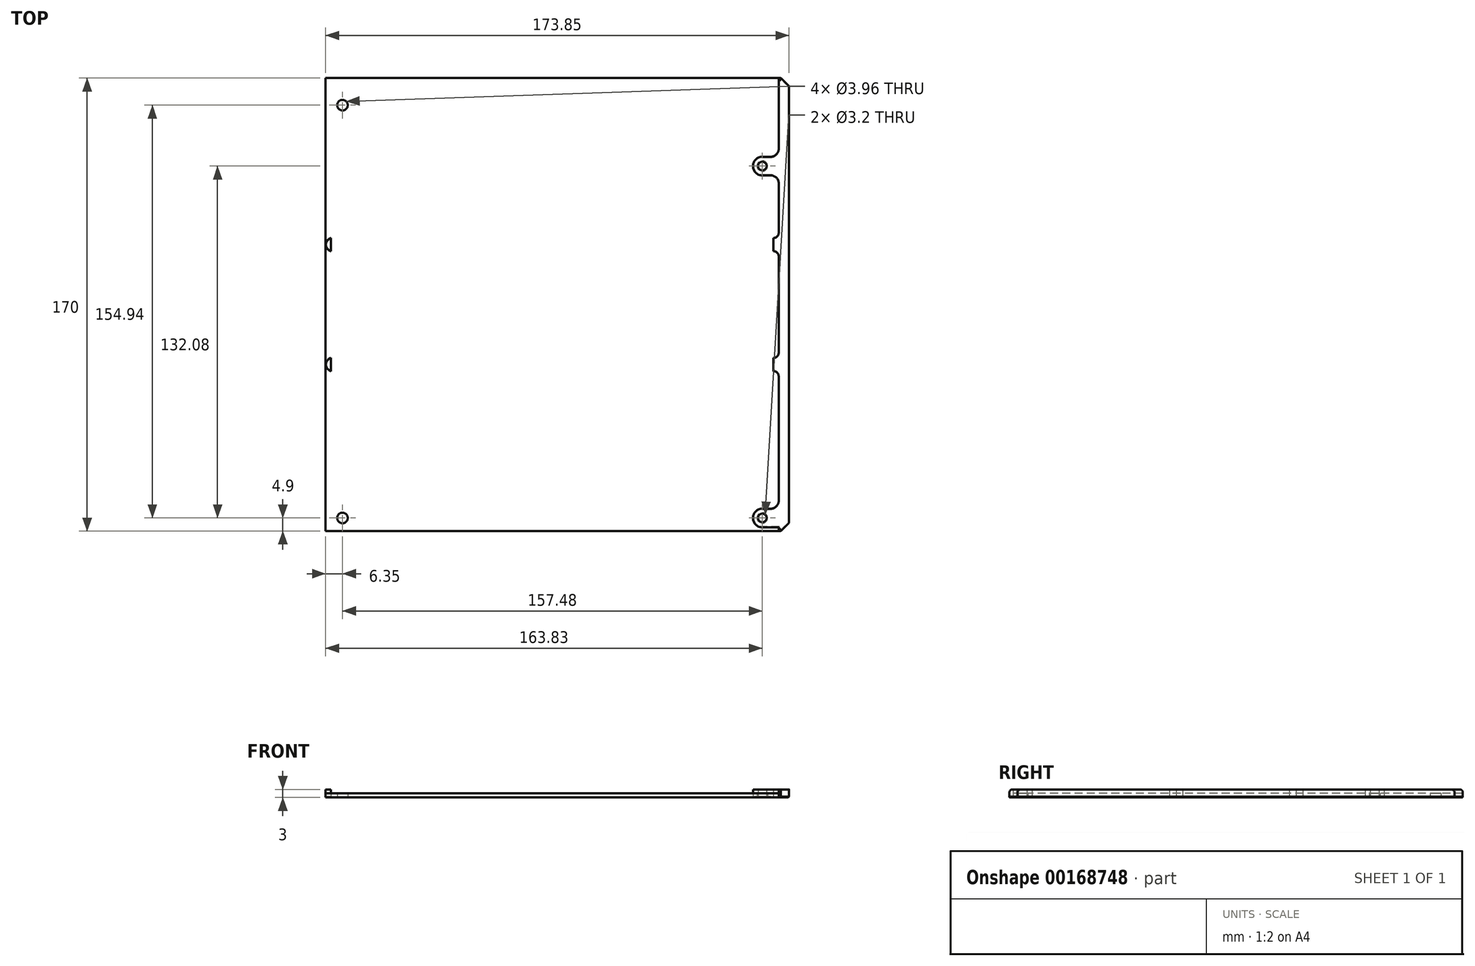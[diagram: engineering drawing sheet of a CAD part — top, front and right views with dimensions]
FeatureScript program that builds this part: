
annotation { "Feature Type Name" : "Feature", "Feature Type Description" : "" }
export const myFeature = defineFeature(function(context is Context, id is Id, definition is map)
    precondition{}
    {
        {
            var Q0;
            Q0=qCreatedBy(makeId("Top.planeOp"),FACE);
            var sketch = newSketch(context, id + "F8", { "sketchPlane" : qUnion([Q0])});
            skLineSegment(sketch, "E0.bottom", {"start": v(85, 85) * mm, "end": v(-85, 85) * mm});
            skLineSegment(sketch, "E0.top", {"start": v(85, -85) * mm, "end": v(-85, -85) * mm});
            skLineSegment(sketch, "E0.left", {"start": v(85, 85) * mm, "end": v(85, -85) * mm});
            skLineSegment(sketch, "E0.right", {"start": v(-85, 85) * mm, "end": v(-85, -85) * mm});
            skPoint(sketch, "E0.middle", {"position": v(0, 0) * mm});
            skCircle(sketch, "E1", {"center": v(-78.65, 74.84) * mm, "radius": 1.98 * mm});
            skCircle(sketch, "E2", {"center": v(-78.65, -80.1) * mm, "radius": 1.98 * mm});
            skCircle(sketch, "E3", {"center": v(78.83, -80.1) * mm, "radius": 1.98 * mm});
            skCircle(sketch, "E4", {"center": v(78.83, 51.98) * mm, "radius": 1.98 * mm});
            skLineSegment(sketch, "E5", {"start": v(-78.65, 74.84) * mm, "end": v(85, 74.84) * mm, "construction": true});
            skSolve(sketch);
        }
        {
            var Q0;
            Q0=qCreatedBy(makeId("Top.planeOp"),FACE);
            var sketch = newSketch(context, id + "F0", { "sketchPlane" : qUnion([Q0])});
            skPoint(sketch, "E6.0", {"position": v(78.83, 51.98) * mm});
            skPoint(sketch, "E6.1", {"position": v(-78.65, 74.84) * mm});
            skPoint(sketch, "E6.2", {"position": v(-78.65, -80.1) * mm});
            skPoint(sketch, "E6.3", {"position": v(78.83, -80.1) * mm});
            skLineSegment(sketch, "E6.4", {"start": v(-85, 85) * mm, "end": v(-85, -85) * mm, "construction": true});
            skLineSegment(sketch, "E7.0", {"start": v(85, 85) * mm, "end": v(85, -85) * mm, "construction": true});
            skArc(sketch, "E8", {"start": v(-78.65, 78.34) * mm, "mid": v(-75.15, 74.84) * mm, "end": v(-78.65, 71.34) * mm});
            skLineSegment(sketch, "E9", {"start": v(-78.65, 78.34) * mm, "end": v(-85, 78.34) * mm});
            skLineSegment(sketch, "E10", {"start": v(-85, 78.34) * mm, "end": v(-85, 85) * mm});
            skLineSegment(sketch, "E11", {"start": v(-78.65, 71.34) * mm, "end": v(-85, 71.34) * mm});
            skArc(sketch, "E12", {"start": v(-78.65, -76.6) * mm, "mid": v(-75.15, -80.1) * mm, "end": v(-78.65, -83.6) * mm});
            skArc(sketch, "E13", {"start": v(78.83, 55.48) * mm, "mid": v(75.33, 51.98) * mm, "end": v(78.83, 48.48) * mm});
            skArc(sketch, "E14", {"start": v(78.83, -76.6) * mm, "mid": v(75.33, -80.1) * mm, "end": v(78.83, -83.6) * mm});
            skCircle(sketch, "E15", {"center": v(-78.65, 74.84) * mm, "radius": 1.6 * mm});
            skCircle(sketch, "E16", {"center": v(78.83, 51.98) * mm, "radius": 1.6 * mm});
            skCircle(sketch, "E17", {"center": v(-78.65, -80.1) * mm, "radius": 1.6 * mm});
            skCircle(sketch, "E18", {"center": v(78.83, -80.1) * mm, "radius": 1.6 * mm});
            skLineSegment(sketch, "E19", {"start": v(-78.65, -76.6) * mm, "end": v(-85, -76.6) * mm});
            skLineSegment(sketch, "E20", {"start": v(-85, -76.6) * mm, "end": v(-85, 71.34) * mm});
            skLineSegment(sketch, "E21", {"start": v(78.83, 55.48) * mm, "end": v(85, 55.48) * mm});
            skLineSegment(sketch, "E22", {"start": v(85, 55.48) * mm, "end": v(85, 85) * mm});
            skLineSegment(sketch, "E23", {"start": v(78.83, -76.6) * mm, "end": v(85, -76.6) * mm});
            skLineSegment(sketch, "E24", {"start": v(78.83, 48.48) * mm, "end": v(85, 48.48) * mm});
            skLineSegment(sketch, "E25", {"start": v(85, 48.48) * mm, "end": v(85, -76.6) * mm});
            skLineSegment(sketch, "E26", {"start": v(78.83, -83.6) * mm, "end": v(85, -83.6) * mm});
            skLineSegment(sketch, "E27", {"start": v(-78.65, -83.6) * mm, "end": v(-85, -83.6) * mm});
            skLineSegment(sketch, "E28", {"start": v(-85, 85) * mm, "end": v(-88.85, 85) * mm});
            skLineSegment(sketch, "E29", {"start": v(-88.85, 85) * mm, "end": v(-88.85, -85) * mm});
            skLineSegment(sketch, "E30", {"start": v(85, 85) * mm, "end": v(88.85, 85) * mm});
            skLineSegment(sketch, "E31", {"start": v(88.85, 85) * mm, "end": v(88.85, -85) * mm});
            skLineSegment(sketch, "E32", {"start": v(85, -83.6) * mm, "end": v(85, -85) * mm});
            skLineSegment(sketch, "E33", {"start": v(88.85, -85) * mm, "end": v(85, -85) * mm});
            skLineSegment(sketch, "E34", {"start": v(-85, -83.6) * mm, "end": v(-85, -85) * mm});
            skLineSegment(sketch, "E35", {"start": v(-88.85, -85) * mm, "end": v(-85, -85) * mm});
            skLineSegment(sketch, "E36", {"start": v(-85, 25) * mm, "end": v(-83, 25) * mm});
            skLineSegment(sketch, "E37", {"start": v(-83, 25) * mm, "end": v(-83, 20) * mm});
            skLineSegment(sketch, "E38", {"start": v(-83, 20) * mm, "end": v(-85, 20) * mm});
            skLineSegment(sketch, "E39", {"start": v(-85, -20) * mm, "end": v(-83, -20) * mm});
            skLineSegment(sketch, "E40", {"start": v(-83, -20) * mm, "end": v(-83, -25) * mm});
            skLineSegment(sketch, "E41", {"start": v(-83, -25) * mm, "end": v(-85, -25) * mm});
            skLineSegment(sketch, "E42.MirrorCS", {"start": v(85, 25) * mm, "end": v(83, 25) * mm});
            skLineSegment(sketch, "E43.MirrorCS", {"start": v(83, 25) * mm, "end": v(83, 20) * mm});
            skLineSegment(sketch, "E44.MirrorCS", {"start": v(83, 20) * mm, "end": v(85, 20) * mm});
            skLineSegment(sketch, "E45.MirrorCS", {"start": v(85, -20) * mm, "end": v(83, -20) * mm});
            skLineSegment(sketch, "E46.MirrorCS", {"start": v(83, -20) * mm, "end": v(83, -25) * mm});
            skLineSegment(sketch, "E47.MirrorCS", {"start": v(83, -25) * mm, "end": v(85, -25) * mm});
            skSolve(sketch);
        }
        {
            var Q0;
            Q0=makeQuery(id+"F0.imprint","IMPRINT",FACE,{"disambiguationData":[TD([[makeQuery(id+"F0.imprint","IMPRINT",EDGE,{"derivedFrom":sQuery(id+"F0.wireOp",EDGE,"E8")}),-1.0]])]});
            var Q1;
            Q1=makeQuery(id+"F0.imprint","IMPRINT",FACE,{"disambiguationData":[TD([[makeQuery(id+"F0.imprint","IMPRINT",EDGE,{"derivedFrom":sQuery(id+"F0.wireOp",EDGE,"E13")}),1.0]])]});
            var Q2;
            {var subQ0=sQuery(id+"F0.wireOp",EDGE,"E36");Q2=makeQuery(id+"F0.imprint","IMPRINT",FACE,{"disambiguationData":[TD([[makeQuery(id+"F0.imprint","IMPRINT",EDGE,{"derivedFrom":subQ0}),-1.0]])]});}
            var Q3;
            {var subQ0=sQuery(id+"F0.wireOp",EDGE,"E39");Q3=makeQuery(id+"F0.imprint","IMPRINT",FACE,{"disambiguationData":[TD([[makeQuery(id+"F0.imprint","IMPRINT",EDGE,{"derivedFrom":subQ0}),-1.0]])]});}
            var Q4;
            {var subQ0=sQuery(id+"F0.wireOp",EDGE,"E42.MirrorCS");Q4=makeQuery(id+"F0.imprint","IMPRINT",FACE,{"disambiguationData":[TD([[makeQuery(id+"F0.imprint","IMPRINT",EDGE,{"derivedFrom":subQ0}),1.0]])]});}
            var Q5;
            {var subQ0=sQuery(id+"F0.wireOp",EDGE,"E45.MirrorCS");Q5=makeQuery(id+"F0.imprint","IMPRINT",FACE,{"disambiguationData":[TD([[makeQuery(id+"F0.imprint","IMPRINT",EDGE,{"derivedFrom":subQ0}),1.0]])]});}
            extrude(context, id + "F1", {"entities" : qUnion([Q0, Q1, Q2, Q3, Q4, Q5]), "depth" : 3 * mm});
        }
        {
            var Q0;
            Q0=makeQuery(id+"F1.opExtrude","SWEPT_EDGE",EDGE,{"disambiguationData":[OSD([sQuery(id+"F0.wireOp",EDGE,"E29"),sQuery(id+"F0.wireOp",EDGE,"E35")])]});
            var Q1;
            Q1=makeQuery(id+"F1.opExtrude","SWEPT_EDGE",EDGE,{"disambiguationData":[OSD([sQuery(id+"F0.wireOp",EDGE,"E31"),sQuery(id+"F0.wireOp",EDGE,"E33")])]});
            var Q2;
            Q2=makeQuery(id+"F1.opExtrude","SWEPT_EDGE",EDGE,{"disambiguationData":[OSD([sQuery(id+"F0.wireOp",EDGE,"E28"),sQuery(id+"F0.wireOp",EDGE,"E29")])]});
            var Q3;
            Q3=makeQuery(id+"F1.opExtrude","SWEPT_EDGE",EDGE,{"disambiguationData":[OSD([sQuery(id+"F0.wireOp",EDGE,"E30"),sQuery(id+"F0.wireOp",EDGE,"E31")])]});
            chamfer(context, id + "F2", {"entities" : qUnion([Q0, Q1, Q2, Q3]), "width" : 3 * mm});
        }
        {
            var Q0;
            Q0=makeQuery(id+"F1.opExtrude","CAP_EDGE",EDGE,{"disambiguationData":[OSD([sQuery(id+"F0.wireOp",EDGE,"E33")])],"isStart":false});
            var Q1;
            Q1=makeQuery(id+"F1.opExtrude","CAP_EDGE",EDGE,{"disambiguationData":[OSD([sQuery(id+"F0.wireOp",EDGE,"E35")])],"isStart":false});
            var Q2;
            {var subQ0=sQuery(id+"F0.wireOp",EDGE,"E35");var subQ1=sQuery(id+"F0.wireOp",EDGE,"E29");Q2=makeQuery(id+"F2.opChamfer","BLEND_EDGE",EDGE,{"blendedFrom":[makeQuery(id+"F1.opExtrude","SWEPT_EDGE",EDGE,{"disambiguationData":[OSD([subQ1,subQ0])]}),makeQuery(id+"F1.opExtrude","CAP_FACE",FACE,{"disambiguationData":[OSD([sQuery(id+"F0.wireOp",EDGE,"E8"),sQuery(id+"F0.wireOp",EDGE,"E9"),sQuery(id+"F0.wireOp",EDGE,"E10"),sQuery(id+"F0.wireOp",EDGE,"E11"),sQuery(id+"F0.wireOp",EDGE,"E12"),sQuery(id+"F0.wireOp",EDGE,"E15"),sQuery(id+"F0.wireOp",EDGE,"E17"),sQuery(id+"F0.wireOp",EDGE,"E19"),sQuery(id+"F0.wireOp",EDGE,"E20"),sQuery(id+"F0.wireOp",EDGE,"E27"),sQuery(id+"F0.wireOp",EDGE,"E28"),subQ1,sQuery(id+"F0.wireOp",EDGE,"E34"),subQ0,sQuery(id+"F0.wireOp",EDGE,"E36"),sQuery(id+"F0.wireOp",EDGE,"E37"),sQuery(id+"F0.wireOp",EDGE,"E38"),sQuery(id+"F0.wireOp",EDGE,"E39"),sQuery(id+"F0.wireOp",EDGE,"E40"),sQuery(id+"F0.wireOp",EDGE,"E41")])],"isStart":false})],"blendedInto":[makeQuery(id+"F1.opExtrude","CAP_FACE",FACE,{"disambiguationData":[OSD([sQuery(id+"F0.wireOp",EDGE,"E8"),sQuery(id+"F0.wireOp",EDGE,"E9"),sQuery(id+"F0.wireOp",EDGE,"E10"),sQuery(id+"F0.wireOp",EDGE,"E11"),sQuery(id+"F0.wireOp",EDGE,"E12"),sQuery(id+"F0.wireOp",EDGE,"E15"),sQuery(id+"F0.wireOp",EDGE,"E17"),sQuery(id+"F0.wireOp",EDGE,"E19"),sQuery(id+"F0.wireOp",EDGE,"E20"),sQuery(id+"F0.wireOp",EDGE,"E27"),sQuery(id+"F0.wireOp",EDGE,"E28"),subQ1,sQuery(id+"F0.wireOp",EDGE,"E34"),subQ0,sQuery(id+"F0.wireOp",EDGE,"E36"),sQuery(id+"F0.wireOp",EDGE,"E37"),sQuery(id+"F0.wireOp",EDGE,"E38"),sQuery(id+"F0.wireOp",EDGE,"E39"),sQuery(id+"F0.wireOp",EDGE,"E40"),sQuery(id+"F0.wireOp",EDGE,"E41")])],"isStart":false})]});}
            var Q3;
            {var subQ0=sQuery(id+"F0.wireOp",EDGE,"E33");var subQ1=sQuery(id+"F0.wireOp",EDGE,"E31");Q3=makeQuery(id+"F2.opChamfer","BLEND_EDGE",EDGE,{"blendedFrom":[makeQuery(id+"F1.opExtrude","SWEPT_EDGE",EDGE,{"disambiguationData":[OSD([subQ1,subQ0])]}),makeQuery(id+"F1.opExtrude","CAP_FACE",FACE,{"disambiguationData":[OSD([sQuery(id+"F0.wireOp",EDGE,"E13"),sQuery(id+"F0.wireOp",EDGE,"E14"),sQuery(id+"F0.wireOp",EDGE,"E16"),sQuery(id+"F0.wireOp",EDGE,"E18"),sQuery(id+"F0.wireOp",EDGE,"E21"),sQuery(id+"F0.wireOp",EDGE,"E22"),sQuery(id+"F0.wireOp",EDGE,"E23"),sQuery(id+"F0.wireOp",EDGE,"E24"),sQuery(id+"F0.wireOp",EDGE,"E25"),sQuery(id+"F0.wireOp",EDGE,"E26"),sQuery(id+"F0.wireOp",EDGE,"E30"),subQ1,sQuery(id+"F0.wireOp",EDGE,"E32"),subQ0,sQuery(id+"F0.wireOp",EDGE,"E42.MirrorCS"),sQuery(id+"F0.wireOp",EDGE,"E43.MirrorCS"),sQuery(id+"F0.wireOp",EDGE,"E44.MirrorCS"),sQuery(id+"F0.wireOp",EDGE,"E45.MirrorCS"),sQuery(id+"F0.wireOp",EDGE,"E46.MirrorCS"),sQuery(id+"F0.wireOp",EDGE,"E47.MirrorCS")])],"isStart":false})],"blendedInto":[makeQuery(id+"F1.opExtrude","CAP_FACE",FACE,{"disambiguationData":[OSD([sQuery(id+"F0.wireOp",EDGE,"E13"),sQuery(id+"F0.wireOp",EDGE,"E14"),sQuery(id+"F0.wireOp",EDGE,"E16"),sQuery(id+"F0.wireOp",EDGE,"E18"),sQuery(id+"F0.wireOp",EDGE,"E21"),sQuery(id+"F0.wireOp",EDGE,"E22"),sQuery(id+"F0.wireOp",EDGE,"E23"),sQuery(id+"F0.wireOp",EDGE,"E24"),sQuery(id+"F0.wireOp",EDGE,"E25"),sQuery(id+"F0.wireOp",EDGE,"E26"),sQuery(id+"F0.wireOp",EDGE,"E30"),subQ1,sQuery(id+"F0.wireOp",EDGE,"E32"),subQ0,sQuery(id+"F0.wireOp",EDGE,"E42.MirrorCS"),sQuery(id+"F0.wireOp",EDGE,"E43.MirrorCS"),sQuery(id+"F0.wireOp",EDGE,"E44.MirrorCS"),sQuery(id+"F0.wireOp",EDGE,"E45.MirrorCS"),sQuery(id+"F0.wireOp",EDGE,"E46.MirrorCS"),sQuery(id+"F0.wireOp",EDGE,"E47.MirrorCS")])],"isStart":false})]});}
            var Q4;
            Q4=makeQuery(id+"F1.opExtrude","CAP_EDGE",EDGE,{"disambiguationData":[OSD([sQuery(id+"F0.wireOp",EDGE,"E28")])],"isStart":false});
            var Q5;
            {var subQ0=sQuery(id+"F0.wireOp",EDGE,"E29");var subQ1=sQuery(id+"F0.wireOp",EDGE,"E28");Q5=makeQuery(id+"F2.opChamfer","BLEND_EDGE",EDGE,{"blendedFrom":[makeQuery(id+"F1.opExtrude","SWEPT_EDGE",EDGE,{"disambiguationData":[OSD([subQ1,subQ0])]}),makeQuery(id+"F1.opExtrude","CAP_FACE",FACE,{"disambiguationData":[OSD([sQuery(id+"F0.wireOp",EDGE,"E8"),sQuery(id+"F0.wireOp",EDGE,"E9"),sQuery(id+"F0.wireOp",EDGE,"E10"),sQuery(id+"F0.wireOp",EDGE,"E11"),sQuery(id+"F0.wireOp",EDGE,"E12"),sQuery(id+"F0.wireOp",EDGE,"E15"),sQuery(id+"F0.wireOp",EDGE,"E17"),sQuery(id+"F0.wireOp",EDGE,"E19"),sQuery(id+"F0.wireOp",EDGE,"E20"),sQuery(id+"F0.wireOp",EDGE,"E27"),subQ1,subQ0,sQuery(id+"F0.wireOp",EDGE,"E34"),sQuery(id+"F0.wireOp",EDGE,"E35"),sQuery(id+"F0.wireOp",EDGE,"E36"),sQuery(id+"F0.wireOp",EDGE,"E37"),sQuery(id+"F0.wireOp",EDGE,"E38"),sQuery(id+"F0.wireOp",EDGE,"E39"),sQuery(id+"F0.wireOp",EDGE,"E40"),sQuery(id+"F0.wireOp",EDGE,"E41")])],"isStart":false})],"blendedInto":[makeQuery(id+"F1.opExtrude","CAP_FACE",FACE,{"disambiguationData":[OSD([sQuery(id+"F0.wireOp",EDGE,"E8"),sQuery(id+"F0.wireOp",EDGE,"E9"),sQuery(id+"F0.wireOp",EDGE,"E10"),sQuery(id+"F0.wireOp",EDGE,"E11"),sQuery(id+"F0.wireOp",EDGE,"E12"),sQuery(id+"F0.wireOp",EDGE,"E15"),sQuery(id+"F0.wireOp",EDGE,"E17"),sQuery(id+"F0.wireOp",EDGE,"E19"),sQuery(id+"F0.wireOp",EDGE,"E20"),sQuery(id+"F0.wireOp",EDGE,"E27"),subQ1,subQ0,sQuery(id+"F0.wireOp",EDGE,"E34"),sQuery(id+"F0.wireOp",EDGE,"E35"),sQuery(id+"F0.wireOp",EDGE,"E36"),sQuery(id+"F0.wireOp",EDGE,"E37"),sQuery(id+"F0.wireOp",EDGE,"E38"),sQuery(id+"F0.wireOp",EDGE,"E39"),sQuery(id+"F0.wireOp",EDGE,"E40"),sQuery(id+"F0.wireOp",EDGE,"E41")])],"isStart":false})]});}
            var Q6;
            {var subQ0=sQuery(id+"F0.wireOp",EDGE,"E31");var subQ1=sQuery(id+"F0.wireOp",EDGE,"E30");Q6=makeQuery(id+"F2.opChamfer","BLEND_EDGE",EDGE,{"blendedFrom":[makeQuery(id+"F1.opExtrude","SWEPT_EDGE",EDGE,{"disambiguationData":[OSD([subQ1,subQ0])]}),makeQuery(id+"F1.opExtrude","CAP_FACE",FACE,{"disambiguationData":[OSD([sQuery(id+"F0.wireOp",EDGE,"E13"),sQuery(id+"F0.wireOp",EDGE,"E14"),sQuery(id+"F0.wireOp",EDGE,"E16"),sQuery(id+"F0.wireOp",EDGE,"E18"),sQuery(id+"F0.wireOp",EDGE,"E21"),sQuery(id+"F0.wireOp",EDGE,"E22"),sQuery(id+"F0.wireOp",EDGE,"E23"),sQuery(id+"F0.wireOp",EDGE,"E24"),sQuery(id+"F0.wireOp",EDGE,"E25"),sQuery(id+"F0.wireOp",EDGE,"E26"),subQ1,subQ0,sQuery(id+"F0.wireOp",EDGE,"E32"),sQuery(id+"F0.wireOp",EDGE,"E33"),sQuery(id+"F0.wireOp",EDGE,"E42.MirrorCS"),sQuery(id+"F0.wireOp",EDGE,"E43.MirrorCS"),sQuery(id+"F0.wireOp",EDGE,"E44.MirrorCS"),sQuery(id+"F0.wireOp",EDGE,"E45.MirrorCS"),sQuery(id+"F0.wireOp",EDGE,"E46.MirrorCS"),sQuery(id+"F0.wireOp",EDGE,"E47.MirrorCS")])],"isStart":false})],"blendedInto":[makeQuery(id+"F1.opExtrude","CAP_FACE",FACE,{"disambiguationData":[OSD([sQuery(id+"F0.wireOp",EDGE,"E13"),sQuery(id+"F0.wireOp",EDGE,"E14"),sQuery(id+"F0.wireOp",EDGE,"E16"),sQuery(id+"F0.wireOp",EDGE,"E18"),sQuery(id+"F0.wireOp",EDGE,"E21"),sQuery(id+"F0.wireOp",EDGE,"E22"),sQuery(id+"F0.wireOp",EDGE,"E23"),sQuery(id+"F0.wireOp",EDGE,"E24"),sQuery(id+"F0.wireOp",EDGE,"E25"),sQuery(id+"F0.wireOp",EDGE,"E26"),subQ1,subQ0,sQuery(id+"F0.wireOp",EDGE,"E32"),sQuery(id+"F0.wireOp",EDGE,"E33"),sQuery(id+"F0.wireOp",EDGE,"E42.MirrorCS"),sQuery(id+"F0.wireOp",EDGE,"E43.MirrorCS"),sQuery(id+"F0.wireOp",EDGE,"E44.MirrorCS"),sQuery(id+"F0.wireOp",EDGE,"E45.MirrorCS"),sQuery(id+"F0.wireOp",EDGE,"E46.MirrorCS"),sQuery(id+"F0.wireOp",EDGE,"E47.MirrorCS")])],"isStart":false})]});}
            var Q7;
            Q7=makeQuery(id+"F1.opExtrude","CAP_EDGE",EDGE,{"disambiguationData":[OSD([sQuery(id+"F0.wireOp",EDGE,"E30")])],"isStart":false});
            fillet(context, id + "F3", {"entities" : qUnion([Q0, Q1, Q2, Q3, Q4, Q5, Q6, Q7]), "radius" : 1 * mm, "allowEdgeOverflow" : false});
        }
        {
            var Q0;
            Q0=makeQuery(id+"F1.opExtrude","SWEPT_EDGE",EDGE,{"disambiguationData":[OSD([sQuery(id+"F0.wireOp",EDGE,"E19"),sQuery(id+"F0.wireOp",EDGE,"E20")])]});
            var Q1;
            Q1=makeQuery(id+"F1.opExtrude","SWEPT_EDGE",EDGE,{"disambiguationData":[OSD([sQuery(id+"F0.wireOp",EDGE,"E23"),sQuery(id+"F0.wireOp",EDGE,"E25")])]});
            var Q2;
            Q2=makeQuery(id+"F1.opExtrude","SWEPT_EDGE",EDGE,{"disambiguationData":[OSD([sQuery(id+"F0.wireOp",EDGE,"E24"),sQuery(id+"F0.wireOp",EDGE,"E25")])]});
            var Q3;
            Q3=makeQuery(id+"F1.opExtrude","SWEPT_EDGE",EDGE,{"disambiguationData":[OSD([sQuery(id+"F0.wireOp",EDGE,"E11"),sQuery(id+"F0.wireOp",EDGE,"E20")])]});
            var Q4;
            Q4=makeQuery(id+"F1.opExtrude","SWEPT_EDGE",EDGE,{"disambiguationData":[OSD([sQuery(id+"F0.wireOp",EDGE,"E9"),sQuery(id+"F0.wireOp",EDGE,"E10")])]});
            var Q5;
            Q5=makeQuery(id+"F1.opExtrude","SWEPT_EDGE",EDGE,{"disambiguationData":[OSD([sQuery(id+"F0.wireOp",EDGE,"E21"),sQuery(id+"F0.wireOp",EDGE,"E22")])]});
            fillet(context, id + "F4", {"entities" : qUnion([Q0, Q1, Q2, Q3, Q4, Q5]), "radius" : 3 * mm, "allowEdgeOverflow" : false});
        }
        {
            var Q0;
            Q0=makeQuery(id+"F1.opExtrude","SWEPT_EDGE",EDGE,{"disambiguationData":[OSD([sQuery(id+"F0.wireOp",EDGE,"E20"),sQuery(id+"F0.wireOp",EDGE,"E36")])]});
            var Q1;
            Q1=makeQuery(id+"F1.opExtrude","SWEPT_EDGE",EDGE,{"disambiguationData":[OSD([sQuery(id+"F0.wireOp",EDGE,"E20"),sQuery(id+"F0.wireOp",EDGE,"E38")])]});
            var Q2;
            Q2=makeQuery(id+"F1.opExtrude","SWEPT_EDGE",EDGE,{"disambiguationData":[OSD([sQuery(id+"F0.wireOp",EDGE,"E20"),sQuery(id+"F0.wireOp",EDGE,"E41")])]});
            var Q3;
            Q3=makeQuery(id+"F1.opExtrude","SWEPT_EDGE",EDGE,{"disambiguationData":[OSD([sQuery(id+"F0.wireOp",EDGE,"E20"),sQuery(id+"F0.wireOp",EDGE,"E39")])]});
            var Q4;
            Q4=makeQuery(id+"F1.opExtrude","SWEPT_EDGE",EDGE,{"disambiguationData":[OSD([sQuery(id+"F0.wireOp",EDGE,"E25"),sQuery(id+"F0.wireOp",EDGE,"E47.MirrorCS")])]});
            var Q5;
            Q5=makeQuery(id+"F1.opExtrude","SWEPT_EDGE",EDGE,{"disambiguationData":[OSD([sQuery(id+"F0.wireOp",EDGE,"E25"),sQuery(id+"F0.wireOp",EDGE,"E44.MirrorCS")])]});
            var Q6;
            Q6=makeQuery(id+"F1.opExtrude","SWEPT_EDGE",EDGE,{"disambiguationData":[OSD([sQuery(id+"F0.wireOp",EDGE,"E25"),sQuery(id+"F0.wireOp",EDGE,"E45.MirrorCS")])]});
            var Q7;
            Q7=makeQuery(id+"F1.opExtrude","SWEPT_EDGE",EDGE,{"disambiguationData":[OSD([sQuery(id+"F0.wireOp",EDGE,"E25"),sQuery(id+"F0.wireOp",EDGE,"E42.MirrorCS")])]});
            fillet(context, id + "F5", {"entities" : qUnion([Q0, Q1, Q2, Q3, Q4, Q5, Q6, Q7]), "radius" : 2 * mm, "allowEdgeOverflow" : false});
        }
        {
            var Q0;
            Q0=makeQuery(id+"F1.opExtrude","CAP_FACE",FACE,{"disambiguationData":[OSD([sQuery(id+"F0.wireOp",EDGE,"E13"),sQuery(id+"F0.wireOp",EDGE,"E14"),sQuery(id+"F0.wireOp",EDGE,"E16"),sQuery(id+"F0.wireOp",EDGE,"E18"),sQuery(id+"F0.wireOp",EDGE,"E21"),sQuery(id+"F0.wireOp",EDGE,"E22"),sQuery(id+"F0.wireOp",EDGE,"E23"),sQuery(id+"F0.wireOp",EDGE,"E24"),sQuery(id+"F0.wireOp",EDGE,"E25"),sQuery(id+"F0.wireOp",EDGE,"E26"),sQuery(id+"F0.wireOp",EDGE,"E30"),sQuery(id+"F0.wireOp",EDGE,"E31"),sQuery(id+"F0.wireOp",EDGE,"E32"),sQuery(id+"F0.wireOp",EDGE,"E33")])],"isStart":true});
            var Q1;
            Q1=makeQuery(id+"F1.opExtrude","CAP_FACE",FACE,{"disambiguationData":[OSD([sQuery(id+"F0.wireOp",EDGE,"E8"),sQuery(id+"F0.wireOp",EDGE,"E9"),sQuery(id+"F0.wireOp",EDGE,"E10"),sQuery(id+"F0.wireOp",EDGE,"E11"),sQuery(id+"F0.wireOp",EDGE,"E12"),sQuery(id+"F0.wireOp",EDGE,"E15"),sQuery(id+"F0.wireOp",EDGE,"E17"),sQuery(id+"F0.wireOp",EDGE,"E19"),sQuery(id+"F0.wireOp",EDGE,"E20"),sQuery(id+"F0.wireOp",EDGE,"E27"),sQuery(id+"F0.wireOp",EDGE,"E28"),sQuery(id+"F0.wireOp",EDGE,"E29"),sQuery(id+"F0.wireOp",EDGE,"E34"),sQuery(id+"F0.wireOp",EDGE,"E35")])],"isStart":true});
            chamfer(context, id + "F6", {"entities" : qUnion([Q0, Q1]), "width" : 0.25 * mm});
        }
        {
            var Q0;
            Q0 = qSketchRegion(id + "F8", true);
            extrude(context, id + "F7", {"entities" : qUnion([Q0]), "depth" : 1.6 * mm});
        }
    });
